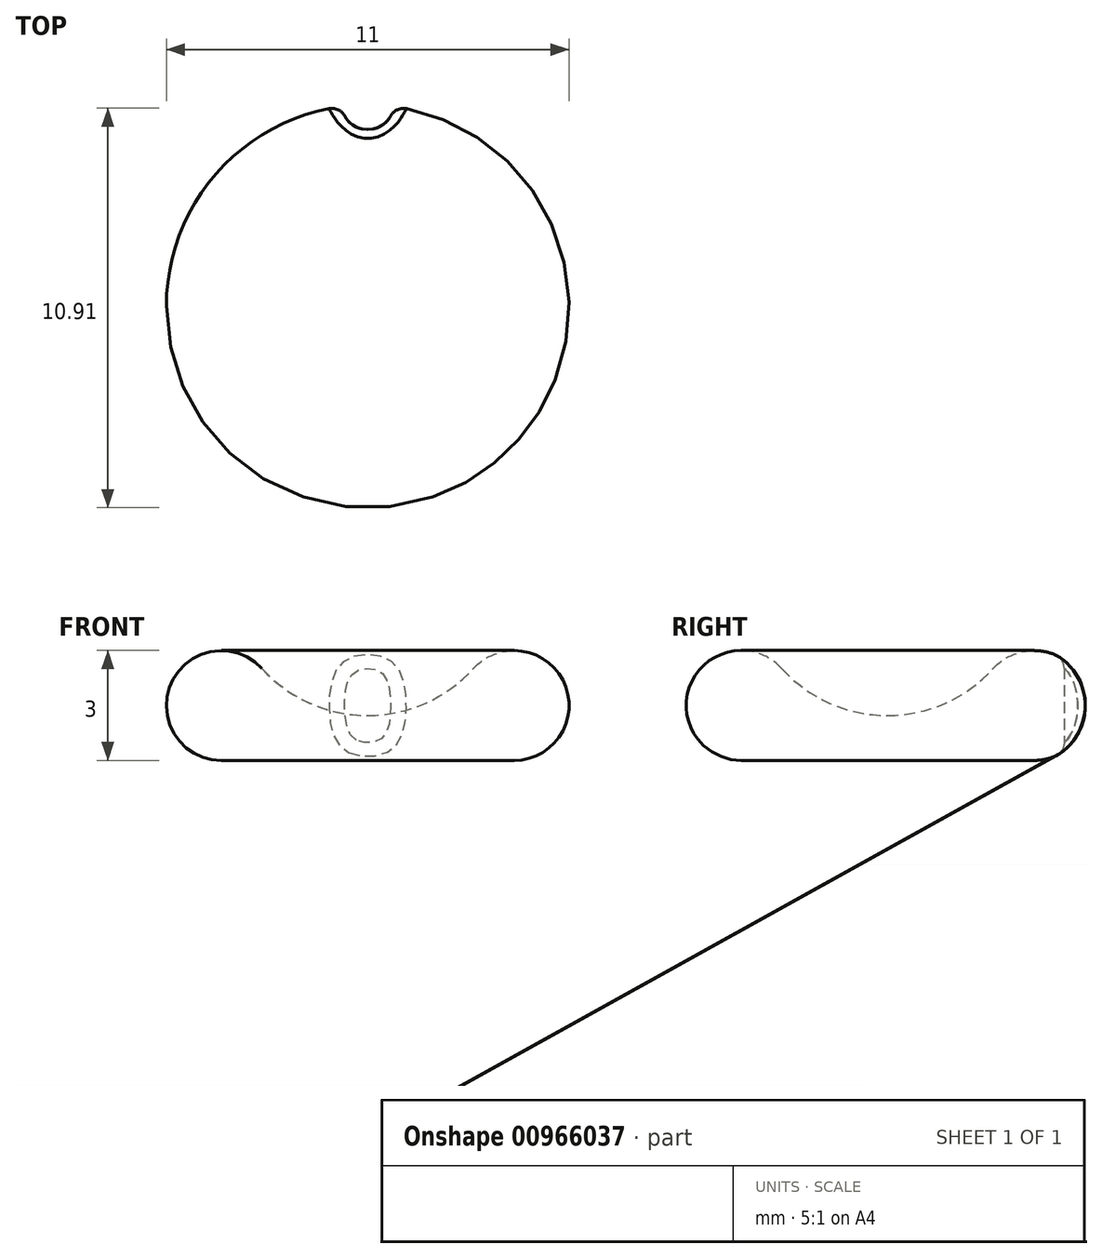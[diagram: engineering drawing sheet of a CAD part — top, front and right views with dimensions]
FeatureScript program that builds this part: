
annotation { "Feature Type Name" : "Feature", "Feature Type Description" : "" }
export const myFeature = defineFeature(function(context is Context, id is Id, definition is map)
    precondition{}
    {
        {
            var Q0;
            Q0=qCreatedBy(makeId("Front.planeOp"),FACE);
            var sketch = newSketch(context, id + "F0", { "sketchPlane" : qUnion([Q0])});
            skCircle(sketch, "E0", {"center": v(-4, 1.5) * mm, "radius": 1.5 * mm});
            skArc(sketch, "E1", {"start": v(-2.89, 2.5) * mm, "mid": v(-1.58, 1.56) * mm, "end": v(0, 1.23) * mm});
            skLineSegment(sketch, "E2", {"start": v(-4.23, 0) * mm, "end": v(0, 0) * mm});
            skLineSegment(sketch, "E3", {"start": v(0, 0) * mm, "end": v(0, 1.23) * mm});
            skSolve(sketch);
        }
        {
            var Q0;
            Q0 = qSketchRegion(id + "F0", true);
            var Q1;
            Q1=sQuery(id+"F0.wireOp",EDGE,"E3");
            revolve(context, id + "F1", {"surfaceOperationType" : NewSurfaceOperationType.NEW, "entities" : qUnion([Q0]), "axis" : qUnion([Q1]), "revolveType" : RevolveType.FULL});
        }
        {
            var Q0;
            Q0=qCreatedBy(makeId("Top.planeOp"),FACE);
            var sketch = newSketch(context, id + "F2", { "sketchPlane" : qUnion([Q0])});
            skCircle(sketch, "E4", {"center": v(0, 5.54) * mm, "radius": 0.72 * mm});
            skSolve(sketch);
        }
        {
            var Q0;
            Q0 = qSketchRegion(id + "F2", true);
            extrude(context, id + "F3", {"entities" : qUnion([Q0]), "operationType" : NewBodyOperationType.REMOVE, "depth" : 25 * mm, "offsetDistance" : 25 * mm});
        }
        {
            var Q0;
            Q0=makeQuery(id+"F3.boolean.opBoolean","INTERSECT",EDGE,{"derivedFrom":[makeQuery(id+"F1.opRevolve","SWEPT_FACE",FACE,{"disambiguationData":[OSD([sQuery(id+"F0.wireOp",EDGE,"E0")])]}),makeQuery(id+"F3.opExtrude","SWEPT_FACE",FACE,{"disambiguationData":[OSD([sQuery(id+"F2.wireOp",EDGE,"E4")])]})]});
            fillet(context, id + "F4", {"entities" : qUnion([Q0]), "radius" : .4 * mm, "tangentPropagation" : true, "allowEdgeOverflow" : false});
        }
    });
